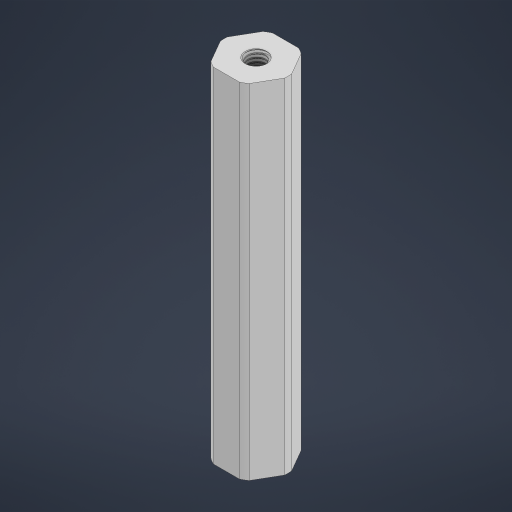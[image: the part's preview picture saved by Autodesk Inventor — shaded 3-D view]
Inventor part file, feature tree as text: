
AUTODESK INVENTOR PART (.ipt)
format: ipt  version: 2023 (Build 270158000, 158)  size: 1,020,416 bytes
history: native  units: in
note: dims shown in document units (in); Inventor stores cm internally (conversion verified against a paired STEP export)
features: mirror x1
ambient origin geometry x8: Origin, YZ Plane, XZ Plane, XY Plane, X Axis, Y Axis, Z Axis, Center Point
bodies: Solid1 (feature_tree)
feature tree (1):
  mirror  "Mirror2"
